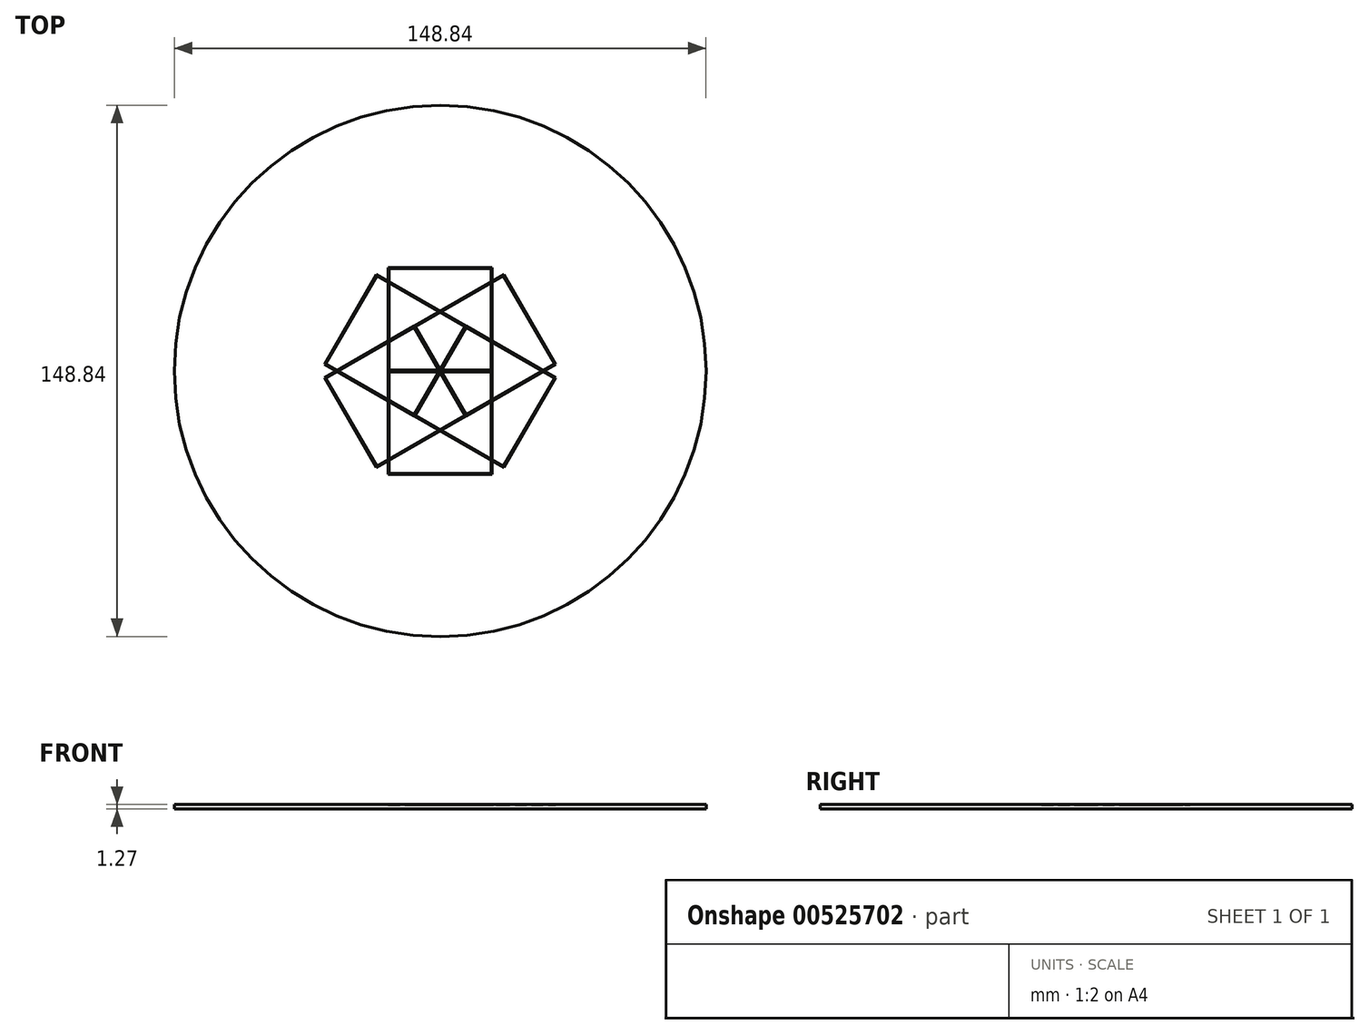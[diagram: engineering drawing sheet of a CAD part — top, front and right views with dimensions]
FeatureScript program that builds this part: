
annotation { "Feature Type Name" : "Feature", "Feature Type Description" : "" }
export const myFeature = defineFeature(function(context is Context, id is Id, definition is map)
    precondition{}
    {
        {
            var Q0;
            Q0=qCreatedBy(makeId("Top.planeOp"),FACE);
            var sketch = newSketch(context, id + "F0", { "sketchPlane" : qUnion([Q0])});
            skCircle(sketch, "E0", {"center": v(0, 0) * mm, "radius": 74.42 * mm});
            skSolve(sketch);
        }
        {
            var Q0;
            Q0 = qSketchRegion(id + "F0", true);
            extrude(context, id + "F1", {"entities" : qUnion([Q0]), "depth" : 1.27 * mm, "offsetDistance" : 25.4 * mm});
        }
        {
            var Q0;
            Q0=makeQuery(id+"F1.opExtrude","CAP_FACE",FACE,{"disambiguationData":[OSD([sQuery(id+"F0.wireOp",EDGE,"E0")])],"isStart":false});
            var sketch = newSketch(context, id + "F2", { "sketchPlane" : qUnion([Q0])});
            skLineSegment(sketch, "E1.bottom", {"start": v(14.5, 0) * mm, "end": v(-14.5, 0) * mm});
            skLineSegment(sketch, "E1.top", {"start": v(14.5, 29) * mm, "end": v(-14.5, 29) * mm});
            skLineSegment(sketch, "E1.left", {"start": v(14.5, 0) * mm, "end": v(14.5, 29) * mm});
            skLineSegment(sketch, "E1.right", {"start": v(-14.5, 0) * mm, "end": v(-14.5, 29) * mm});
            skPoint(sketch, "E1.middle", {"position": v(0, 14.5) * mm});
            skLineSegment(sketch, "E2.0", {"start": v(-14.24, 0.25) * mm, "end": v(-14.24, 28.74) * mm});
            skLineSegment(sketch, "E2.1", {"start": v(14.24, 0.25) * mm, "end": v(-14.24, 0.25) * mm});
            skLineSegment(sketch, "E2.2", {"start": v(14.24, 0.25) * mm, "end": v(14.24, 28.74) * mm});
            skLineSegment(sketch, "E2.3", {"start": v(14.24, 28.74) * mm, "end": v(-14.24, 28.74) * mm});
            skSolve(sketch);
        }
        {
            var Q0;
            Q0 = qSketchRegion(id + "F2", true);
            extrude(context, id + "F3", {"entities" : qUnion([Q0]), "operationType" : NewBodyOperationType.REMOVE, "oppositeDirection" : true, "depth" : 0.25 * mm, "offsetDistance" : 25.4 * mm});
        }
        {
            var Q0;
            Q0=makeQuery(id+"F1.opExtrude","SWEPT_BODY",BODY,{"disambiguationData":[OSD([sQuery(id+"F0.wireOp",EDGE,"E0")])]});
            var Q1;
            Q1=makeQuery(id+"F1.opExtrude","CAP_EDGE",EDGE,{"disambiguationData":[OSD([sQuery(id+"F0.wireOp",EDGE,"E0")])],"isStart":false});
            circularPattern(context, id + "F4", {"entities" : qUnion([Q0]), "axis" : qUnion([Q1]), "angle" : 360 * degree, "instanceCount" : 6, "equalSpace" : true});
        }
    });
